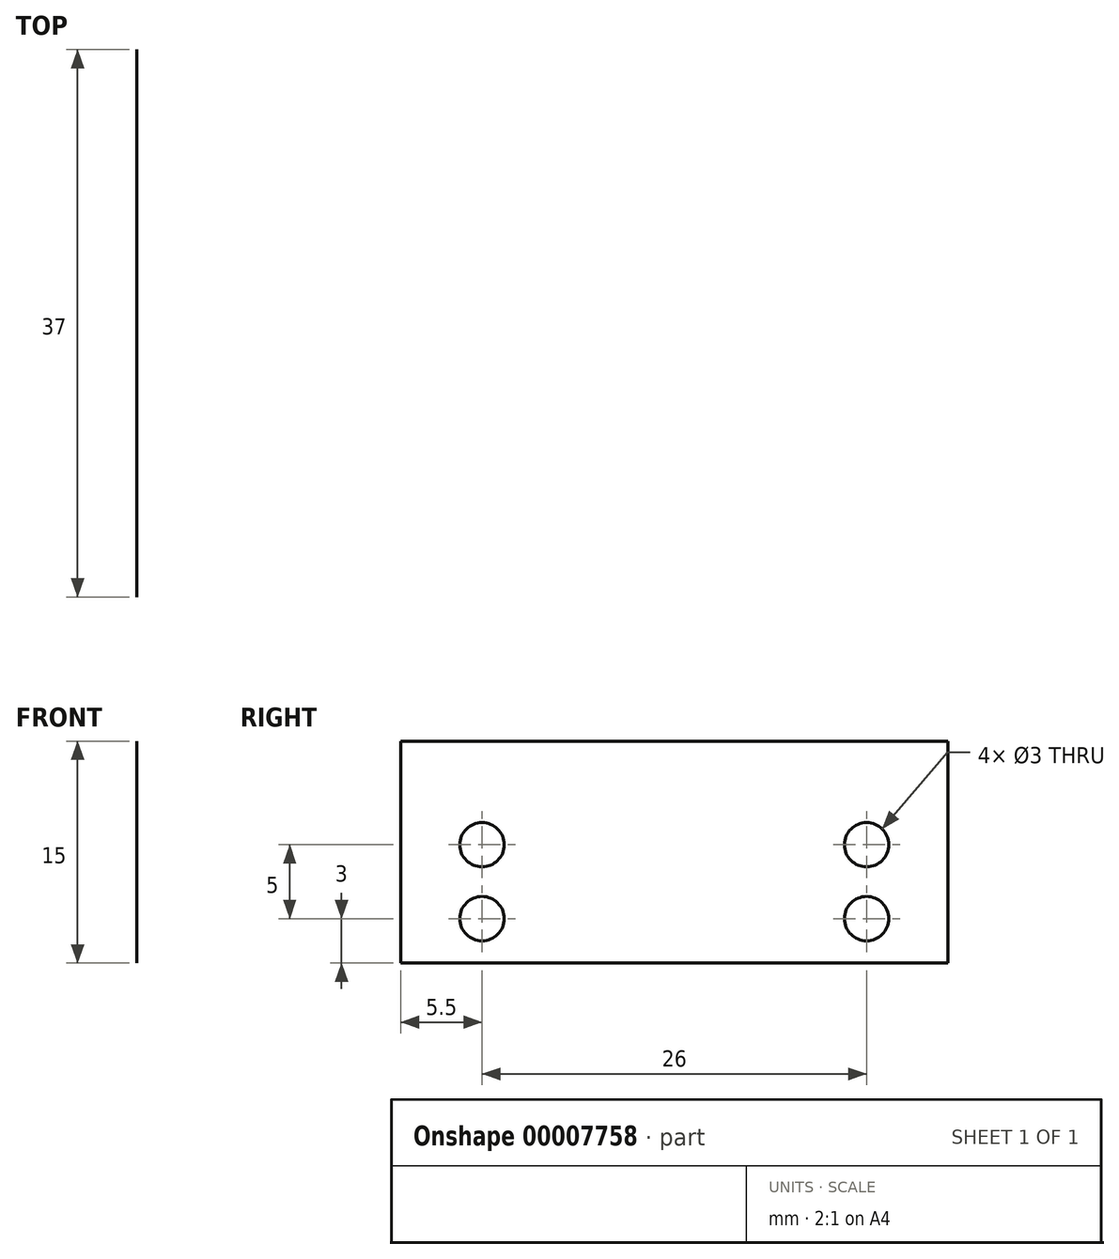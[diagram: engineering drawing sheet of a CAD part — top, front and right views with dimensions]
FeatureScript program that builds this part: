
annotation { "Feature Type Name" : "Feature", "Feature Type Description" : "" }
export const myFeature = defineFeature(function(context is Context, id is Id, definition is map)
    precondition{}
    {
        {
            var Q0;
            Q0=qCreatedBy(makeId("Right.planeOp"),FACE);
            var sketch = newSketch(context, id + "F0", { "sketchPlane" : qUnion([Q0])});
            skLineSegment(sketch, "E0.rect.bottom", {"start": v(-18.5, -7.5) * mm, "end": v(18.5, -7.5) * mm});
            skLineSegment(sketch, "E0.rect.top", {"start": v(-18.5, 7.5) * mm, "end": v(18.5, 7.5) * mm});
            skLineSegment(sketch, "E0.rect.left", {"start": v(-18.5, -7.5) * mm, "end": v(-18.5, 7.5) * mm});
            skLineSegment(sketch, "E0.rect.right", {"start": v(18.5, -7.5) * mm, "end": v(18.5, 7.5) * mm});
            skPoint(sketch, "E0.rect.middle", {"position": v(0, 0) * mm});
            skCircle(sketch, "E1", {"center": v(-13, -4.5) * mm, "radius": 1.5 * mm});
            skCircle(sketch, "E2", {"center": v(-13, 0.5) * mm, "radius": 1.5 * mm});
            skCircle(sketch, "E3", {"center": v(13, 0.5) * mm, "radius": 1.5 * mm});
            skCircle(sketch, "E4", {"center": v(13, -4.5) * mm, "radius": 1.5 * mm});
            skSolve(sketch);
        }
        {
            var Q0;
            Q0 = qSketchRegion(id + "F0", true);
            extrude(context, id + "F1", {"entities" : qUnion([Q0]), "depth" : 1 / 406.4 * mm});
        }
    });
